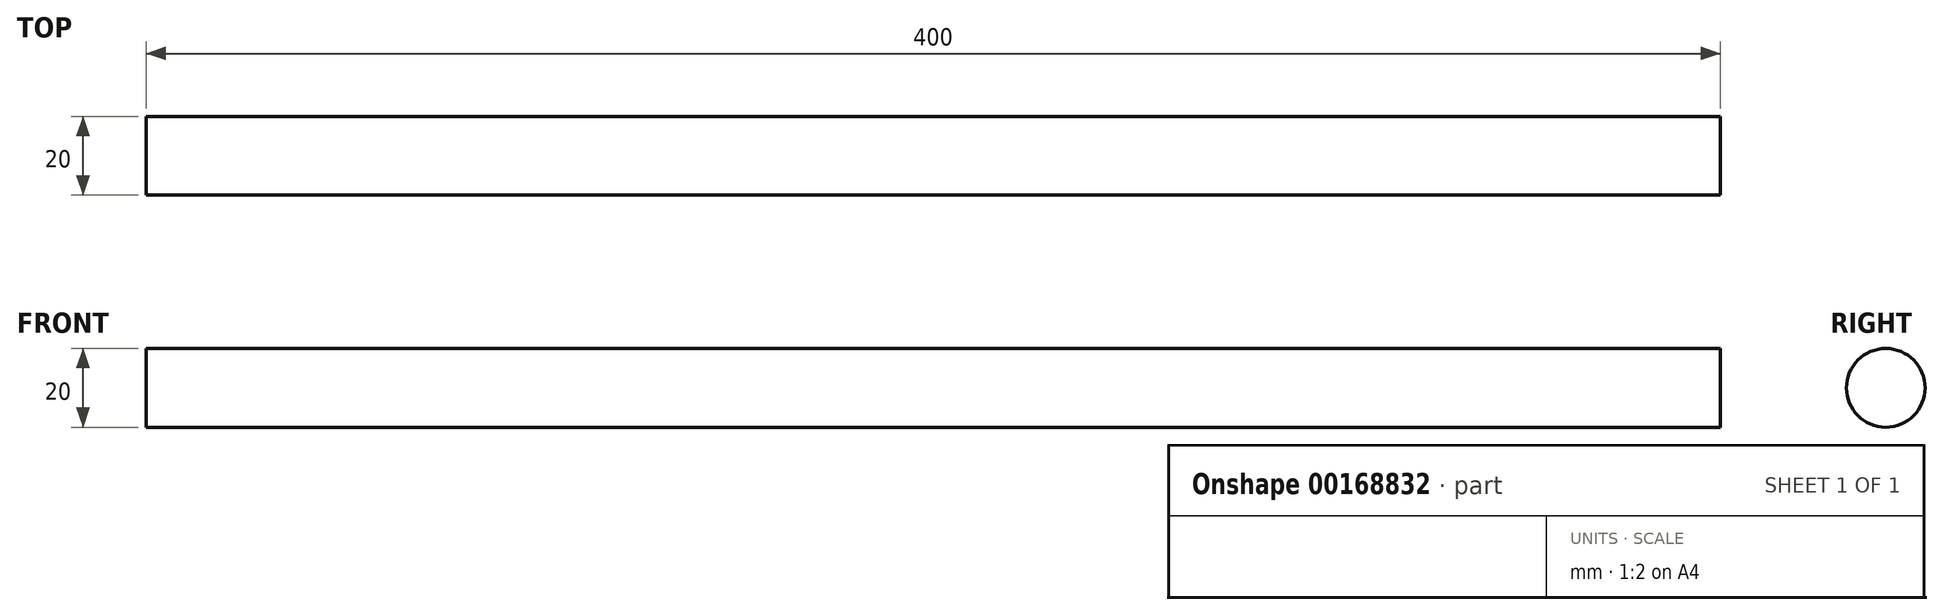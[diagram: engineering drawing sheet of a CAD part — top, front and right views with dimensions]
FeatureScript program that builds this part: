
annotation { "Feature Type Name" : "Feature", "Feature Type Description" : "" }
export const myFeature = defineFeature(function(context is Context, id is Id, definition is map)
    precondition{}
    {
        {
            assignVariable(context, id + "F0", {"name" : "L", "anyValue" : 400 * mm});
        }
        {
            var Q0;
            Q0=qCreatedBy(makeId("Right.planeOp"),FACE);
            var sketch = newSketch(context, id + "F1", { "sketchPlane" : qUnion([Q0])});
            skCircle(sketch, "E0", {"center": v(0, 0) * mm, "radius": 10 * mm});
            skSolve(sketch);
        }
        {
            var Q0;
            Q0=qSketchRegion(id+"F1",true);
            extrude(context, id + "F2", {"entities" : qUnion([Q0]), "oppositeDirection" : true, "depth" : getVariable(context, 'L')});
        }
    });
